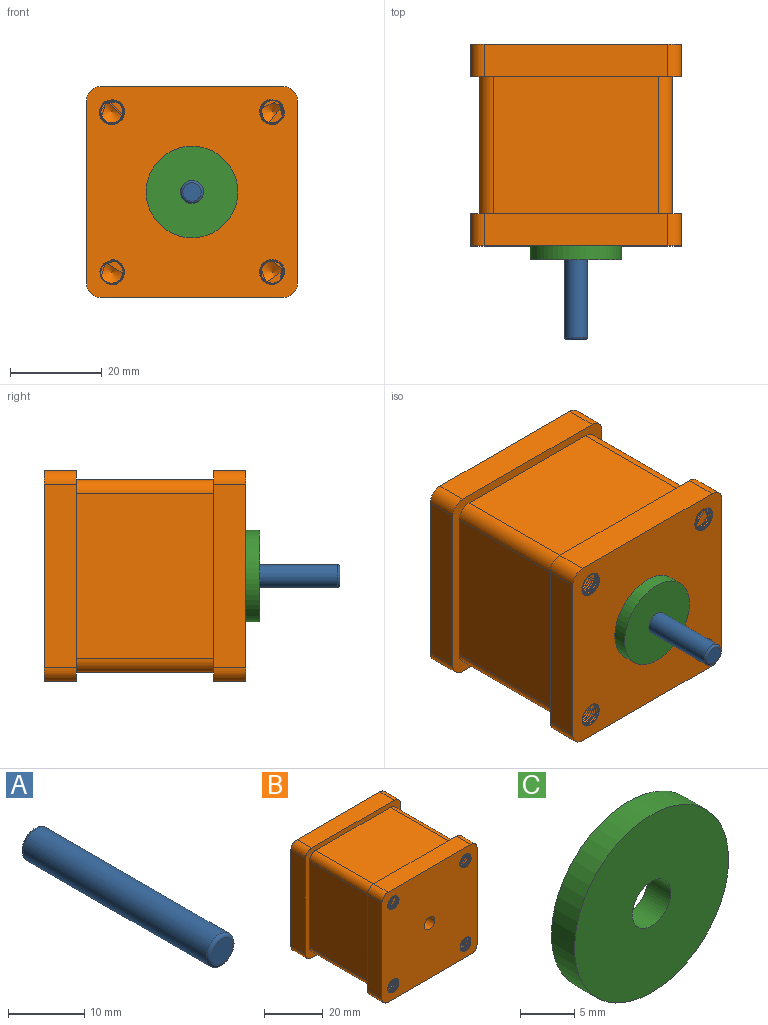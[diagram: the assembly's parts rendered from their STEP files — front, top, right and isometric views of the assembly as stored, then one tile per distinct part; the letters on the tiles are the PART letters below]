
ASSEMBLY  parts=3 mates=2
PART A: 5 faces, bbox 5.4x35x5.4 mm
  f0: cylinder r=2.5mm len=34mm, axis (0,1,0), area 534.1mm2, adj f3,f4
  f1: plane 4x4mm, normal (0,-1,0), area 12.6mm2, adj f4
  f2: plane 4x4mm, normal (0,1,0), area 12.6mm2, adj f3
  f3: torus R=2mm, axis (0,-1,0), area 11.4mm2, adj f0,f2
  f4: torus R=2mm, axis (0,-1,0), area 11.4mm2, adj f0,f1
PART B: 100 faces, bbox 46.2x44.8x46.2 mm
  f0: plane 46.23x46.23mm, normal (0,1,0), area 2024.7mm2, adj f1,f15,f16,f17,f18,f22,f23,f24
  f1: cylinder r=2.5mm len=10mm, axis (0,1,0), area 12mm2, adj f0,f87,f89,f90,f91,f92
  f2: cylinder r=2.5mm len=10mm, axis (0,-1,0), area 12.7mm2, adj f4,f72,f74,f75,f76,f77
  f3: cylinder r=2.5mm len=10mm, axis (0,-1,0), area 25.3mm2, adj f4,f66,f68,f69,f70,f71
  f4: plane 46.23x46.23mm, normal (0,-1,0), area 2002.9mm2, adj f2,f3,f5,f10,f11,f12,f13,f20
  f5: cylinder r=2.5mm len=10mm, axis (0,-1,0), area 12mm2, adj f4,f36,f38,f39,f40,f41
  f6: plane 36x30mm, normal (0,0,1), area 1080mm2, adj f14,f19,f30,f33
  f7: plane 36x30mm, normal (-1,0,0), area 1080mm2, adj f14,f19,f30,f31
  f8: plane 36x30mm, normal (0,0,-1), area 1080mm2, adj f14,f19,f31,f32
  f9: plane 36x30mm, normal (1,0,0), area 1080mm2, adj f14,f19,f32,f33
  f10: plane 40x7mm, normal (0,0,1), area 280mm2, adj f4,f14,f26,f29
  f11: plane 40x7mm, normal (-1,0,0), area 280mm2, adj f4,f14,f26,f27
  f12: plane 40x7mm, normal (0,0,-1), area 280mm2, adj f4,f14,f27,f28
  f13: plane 40x7mm, normal (1,0,0), area 280mm2, adj f4,f14,f28,f29
  f14: plane 46x46mm, normal (0,1,0), area 352mm2, adj f6,f7,f8,f9,f10,f11,f12,f13
  f15: plane 40x7mm, normal (0,0,1), area 280mm2, adj f0,f19,f22,f25
  f16: plane 40x7mm, normal (-1,0,0), area 280mm2, adj f0,f19,f24,f25
  f17: plane 40x7mm, normal (0,0,-1), area 276.9mm2, adj f0,f19,f23,f24,f34
  f18: plane 40x7mm, normal (1,0,0), area 280mm2, adj f0,f19,f22,f23
  f19: plane 46x46mm, normal (0,-1,0), area 352mm2, adj f6,f7,f8,f9,f15,f16,f17,f18
  f20: cylinder r=2.5mm len=7mm, axis (0,-1,0), area 110mm2, adj f4,f21
  f21: plane 5x5mm, normal (0,-1,0), area 19.6mm2, adj f20
  f22: cylinder r=3mm len=7mm, axis (0,-1,0), area 33mm2, adj f0,f15,f18,f19
  f23: cylinder r=3mm len=7mm, axis (0,1,0), area 33mm2, adj f0,f17,f18,f19
  f24: cylinder r=3mm len=7mm, axis (0,-1,0), area 33mm2, adj f0,f16,f17,f19
  f25: cylinder r=3mm len=7mm, axis (0,1,0), area 33mm2, adj f0,f15,f16,f19
  f26: cylinder r=3mm len=7mm, axis (0,-1,0), area 33mm2, adj f4,f10,f11,f14
  f27: cylinder r=3mm len=7mm, axis (0,1,0), area 33mm2, adj f4,f11,f12,f14
  f28: cylinder r=3mm len=7mm, axis (0,-1,0), area 33mm2, adj f4,f12,f13,f14
  f29: cylinder r=3mm len=7mm, axis (0,1,0), area 33mm2, adj f4,f10,f13,f14
  f30: cylinder r=3mm len=30mm, axis (0,-1,0), area 141.4mm2, adj f6,f7,f14,f19
  f31: cylinder r=3mm len=30mm, axis (0,1,0), area 141.4mm2, adj f7,f8,f14,f19
  f32: cylinder r=3mm len=30mm, axis (0,-1,0), area 141.4mm2, adj f8,f9,f14,f19
  f33: cylinder r=3mm len=30mm, axis (0,1,0), area 141.4mm2, adj f6,f9,f14,f19
  f34: cylinder r=1mm len=21mm, axis (0,0,-1), area 131.9mm2, adj f17,f35
  f35: plane 2x2mm, normal (0,0,-1), area 3.1mm2, adj f34
  f36: cone r=0mm half-angle=59deg, axis (0,-1,0), area 22.9mm2, adj f5,f37
  f37: cylinder r=2.5mm len=5mm, axis (0,1,0), area 1.1mm2, adj f36,f39,f41
  f38: plane 0.27x0.27mm, normal (0,0,-1), area 0mm2, adj f4,f5,f41
  f39: plane 0.49x0.27mm, normal (0,0,1), area 0.1mm2, adj f5,f37,f40,f41
  f40: bspline ~10.22x6.41mm, area 116.3mm2, adj f4,f5,f39,f41
  f41: bspline ~10.27x6.41mm, area 126.1mm2, adj f5,f37,f38,f39,f40
  f42: cone r=0mm half-angle=59deg, axis (0,-1,0), area 22.9mm2, adj f62
  f43: cylinder r=2.5mm len=0.8mm, axis (0,-1,0), area 0mm2, adj f4,f44,f64,f65
  f44: cylinder r=2.5mm len=5mm, axis (0,-1,0), area 0.2mm2, adj f43,f45,f64,f65
  f45: cylinder r=2.5mm len=5mm, axis (0,-1,0), area 0.2mm2, adj f44,f46,f64,f65
  f46: cylinder r=2.5mm len=5mm, axis (0,-1,0), area 0.2mm2, adj f45,f47,f64,f65
  f47: cylinder r=2.5mm len=5mm, axis (0,-1,0), area 0.2mm2, adj f46,f48,f64,f65
  f48: cylinder r=2.5mm len=5mm, axis (0,-1,0), area 0.2mm2, adj f47,f49,f64,f65
  f49: cylinder r=2.5mm len=5mm, axis (0,-1,0), area 0.2mm2, adj f48,f50,f64,f65
  f50: cylinder r=2.5mm len=5mm, axis (0,-1,0), area 0.2mm2, adj f49,f51,f64,f65
  f51: cylinder r=2.5mm len=5mm, axis (0,-1,0), area 0.2mm2, adj f50,f52,f64,f65
  f52: cylinder r=2.5mm len=5mm, axis (0,-1,0), area 0.2mm2, adj f51,f53,f64,f65
  f53: cylinder r=2.5mm len=5mm, axis (0,-1,0), area 0.2mm2, adj f52,f54,f64,f65
  f54: cylinder r=2.5mm len=5mm, axis (0,-1,0), area 0.2mm2, adj f53,f55,f64,f65
  f55: cylinder r=2.5mm len=5mm, axis (0,-1,0), area 0.2mm2, adj f54,f56,f64,f65
  f56: cylinder r=2.5mm len=5mm, axis (0,-1,0), area 0.2mm2, adj f55,f57,f64,f65
  f57: cylinder r=2.5mm len=5mm, axis (0,-1,0), area 0.2mm2, adj f56,f58,f64,f65
  f58: cylinder r=2.5mm len=5mm, axis (0,-1,0), area 0.2mm2, adj f57,f59,f64,f65
  f59: cylinder r=2.5mm len=5mm, axis (0,-1,0), area 0.2mm2, adj f58,f60,f64,f65
  f60: cylinder r=2.5mm len=5mm, axis (0,-1,0), area 0.2mm2, adj f59,f61,f64,f65
  f61: cylinder r=2.5mm len=5mm, axis (0,-1,0), area 0.2mm2, adj f60,f62,f64,f65
  f62: cylinder r=2.5mm len=5mm, axis (0,-1,0), area 5.7mm2, adj f42,f61,f63,f64,f65
  f63: plane 0.49x0.27mm, normal (0,0,1), area 0.1mm2, adj f62,f64,f65
  f64: bspline ~9.89x6.41mm, area 111.5mm2, adj f4,f43,f44,f45,f46,f47,f48,f49
  f65: bspline ~10.18x6.41mm, area 123.8mm2, adj f4,f43,f44,f45,f46,f47,f48,f49
  f66: cone r=0mm half-angle=59deg, axis (0,-1,0), area 22.9mm2, adj f3,f67
  f67: cylinder r=2.5mm len=0.54mm, axis (0,-1,0), area 0mm2, adj f66,f68,f71
  f68: plane 0.49x0.27mm, normal (0,0,1), area 0.1mm2, adj f3,f67,f70,f71
  f69: plane 0.02x0.02mm, normal (0,0,-1), area 0mm2, adj f3,f4,f71
  f70: bspline ~9.97x6.41mm, area 113.4mm2, adj f3,f4,f68,f71
  f71: bspline ~10.27x6.41mm, area 124.7mm2, adj f3,f4,f67,f68,f69,f70
  f72: cone r=0mm half-angle=59deg, axis (0,-1,0), area 22.9mm2, adj f2,f73
  f73: cylinder r=2.5mm len=3mm, axis (0,-1,0), area 0.3mm2, adj f72,f74,f77
  f74: plane 0.49x0.27mm, normal (0,0,1), area 0.1mm2, adj f2,f73,f76,f77
  f75: plane 0.15x0.14mm, normal (0,0,-1), area 0mm2, adj f2,f4,f77
  f76: bspline ~10.14x6.41mm, area 114.7mm2, adj f2,f4,f74,f77
  f77: bspline ~10.27x6.41mm, area 126mm2, adj f2,f4,f73,f74,f75,f76
  f78: cone r=0mm half-angle=59deg, axis (0,1,0), area 22.9mm2, adj f79,f80
  f79: cylinder r=2.5mm len=10mm, axis (0,1,0), area -5mm2, adj f0,f78,f81,f82,f83,f84
  f80: cylinder r=2.5mm len=0.54mm, axis (0,-1,0), area 0mm2, adj f78,f82,f83
  f81: plane 0.02x0.02mm, normal (0,0,-1), area 0mm2, adj f0,f79,f83
  f82: plane 0.49x0.27mm, normal (0,0,1), area 0.1mm2, adj f79,f80,f83,f84
  f83: bspline ~10.27x6.41mm, area 125.7mm2, adj f0,f79,f80,f81,f82,f84
  f84: bspline ~10.06x6.41mm, area 113.2mm2, adj f0,f79,f82,f83
  f85: cone r=0mm half-angle=59deg, axis (0,1,0), area 22.9mm2, adj f86
  f86: cylinder r=2.5mm len=10mm, axis (0,1,0), area 157.1mm2, adj f0,f85
  f87: cone r=0mm half-angle=59deg, axis (0,1,0), area 22.9mm2, adj f1,f88
  f88: cylinder r=2.5mm len=5mm, axis (0,-1,0), area 1.1mm2, adj f87,f90,f91
  f89: plane 0.27x0.27mm, normal (0,0,-1), area 0mm2, adj f0,f1,f91
  f90: plane 0.49x0.27mm, normal (0,0,1), area 0.1mm2, adj f1,f88,f91,f92
  f91: bspline ~10.27x6.41mm, area 126.1mm2, adj f1,f88,f89,f90,f92
  f92: bspline ~10.22x6.41mm, area 116.3mm2, adj f0,f1,f90,f91
  f93: cone r=0mm half-angle=59deg, axis (0,1,0), area 22.9mm2, adj f94,f95
  f94: cylinder r=2.5mm len=10mm, axis (0,1,0), area 1.5mm2, adj f0,f93,f96,f97,f98,f99
  f95: cylinder r=2.5mm len=3mm, axis (0,-1,0), area 0.3mm2, adj f93,f97,f98
  f96: plane 0.15x0.14mm, normal (0,0,-1), area 0mm2, adj f0,f94,f98
  f97: plane 0.49x0.27mm, normal (0,0,1), area 0.1mm2, adj f94,f95,f98,f99
  f98: bspline ~10.27x6.41mm, area 126.7mm2, adj f0,f94,f95,f96,f97,f99
  f99: bspline ~10.14x6.41mm, area 114.2mm2, adj f0,f94,f97,f98
PART C: 4 faces, bbox 20x3x20 mm
  f0: cylinder r=10mm len=20mm, axis (0,1,0), area 188.5mm2, adj f1,f2
  f1: plane 20x20mm, normal (0,-1,0), area 294.5mm2, adj f0,f3
  f2: plane 20x20mm, normal (0,1,0), area 294.5mm2, adj f0,f3
  f3: cylinder r=2.5mm len=5mm, axis (0,-1,0), area 47.1mm2, adj f1,f2
PLACE A t=(-6.29,7.5,-87.12)mm
PLACE B rot(axis=(0,-1,0),90deg) t=(-6.29,15,-87.12)mm
PLACE C rot(axis=(0,-1,0),90deg) t=(-6.29,15,-87.12)mm
MATE fastened C.f0 <-> B.f20  axis (0,1,0) through (-6.29,-7,-87.12)mm
MATE revolute C.f3 <-> A.f0  axis (0,-1,0) through (-6.29,-10,-87.12)mm
